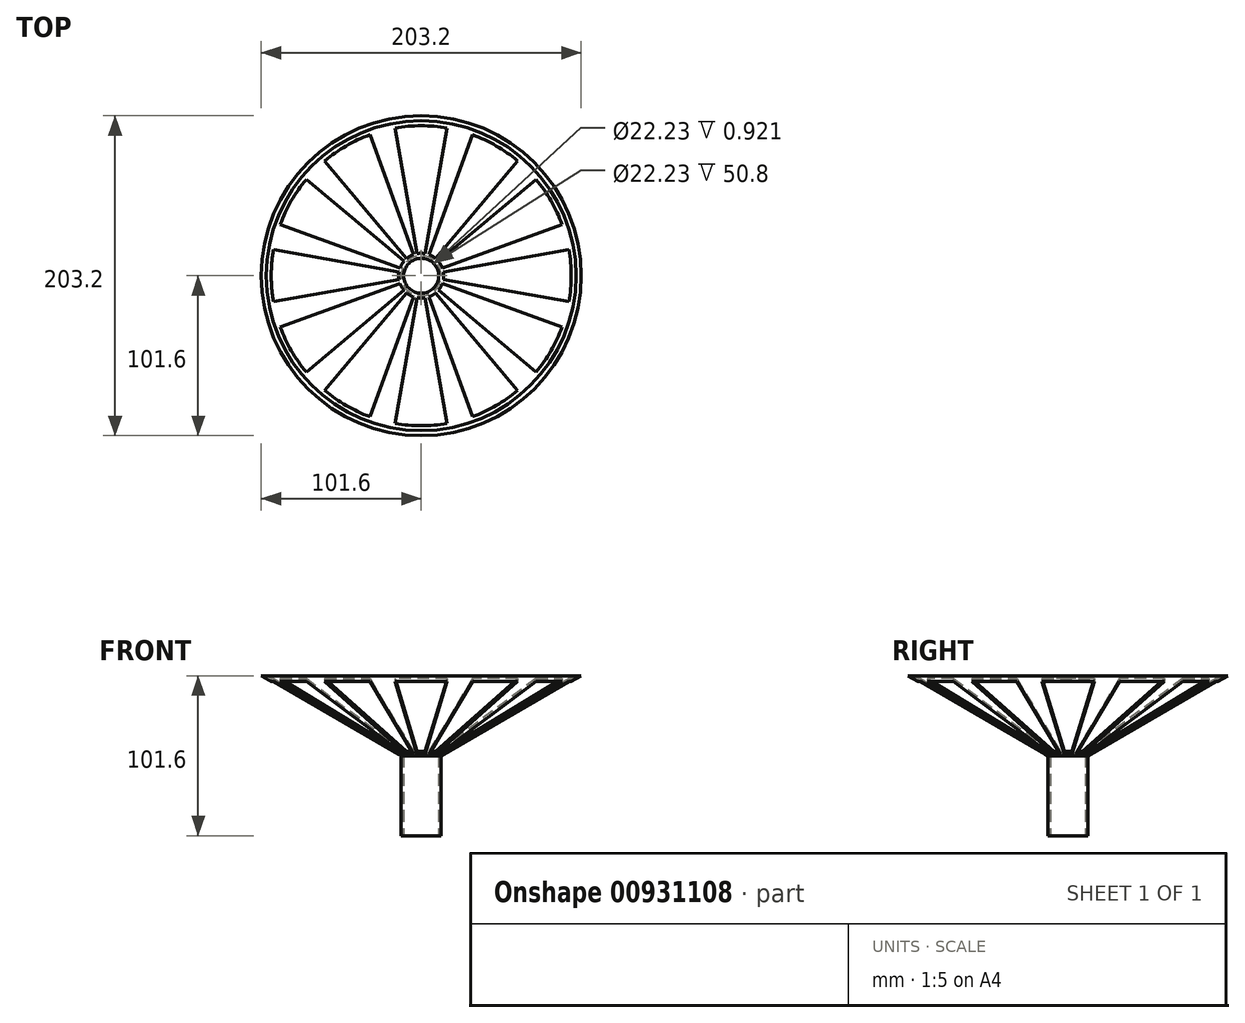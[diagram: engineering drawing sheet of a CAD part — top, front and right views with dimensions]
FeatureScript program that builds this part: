
annotation { "Feature Type Name" : "Feature", "Feature Type Description" : "" }
export const myFeature = defineFeature(function(context is Context, id is Id, definition is map)
    precondition{}
    {
        {
            var Q0;
            Q0=qCreatedBy(makeId("Top.planeOp"),FACE);
            var sketch = newSketch(context, id + "F0", { "sketchPlane" : qUnion([Q0])});
            skCircle(sketch, "E0", {"center": v(0, 0) * mm, "radius": 11.11 * mm});
            skCircle(sketch, "E1", {"center": v(0, 0) * mm, "radius": 12.7 * mm});
            skLineSegment(sketch, "E2", {"start": v(0, 0) * mm, "end": v(0, -95.25) * mm});
            skLineSegment(sketch, "E3", {"start": v(2.48, -14.07) * mm, "end": v(16.54, -93.8) * mm});
            skLineSegment(sketch, "E4", {"start": v(-2.48, -14.07) * mm, "end": v(-16.54, -93.8) * mm});
            skArc(sketch, "E5", {"start": v(-2.48, -14.07) * mm, "mid": v(0, -14.29) * mm, "end": v(2.48, -14.07) * mm});
            skArc(sketch, "E6", {"start": v(-16.54, -93.8) * mm, "mid": v(0, -95.25) * mm, "end": v(16.54, -93.8) * mm});
            skLineSegment(sketch, "E7.1.0", {"start": v(9.18, -10.94) * mm, "end": v(61.23, -72.97) * mm});
            skArc(sketch, "E7.1.1", {"start": v(4.89, -13.43) * mm, "mid": v(7.14, -12.37) * mm, "end": v(9.18, -10.94) * mm});
            skLineSegment(sketch, "E7.1.2", {"start": v(4.89, -13.43) * mm, "end": v(32.58, -89.5) * mm});
            skArc(sketch, "E7.1.3", {"start": v(32.58, -89.5) * mm, "mid": v(47.63, -82.49) * mm, "end": v(61.23, -72.97) * mm});
            skLineSegment(sketch, "E7.2.0", {"start": v(13.43, -4.89) * mm, "end": v(89.5, -32.58) * mm});
            skArc(sketch, "E7.2.1", {"start": v(10.94, -9.18) * mm, "mid": v(12.37, -7.14) * mm, "end": v(13.43, -4.89) * mm});
            skLineSegment(sketch, "E7.2.2", {"start": v(10.94, -9.18) * mm, "end": v(72.97, -61.23) * mm});
            skArc(sketch, "E7.2.3", {"start": v(72.97, -61.23) * mm, "mid": v(82.49, -47.63) * mm, "end": v(89.5, -32.58) * mm});
            skLineSegment(sketch, "E7.3.0", {"start": v(14.07, 2.48) * mm, "end": v(93.8, 16.54) * mm});
            skArc(sketch, "E7.3.1", {"start": v(14.07, -2.48) * mm, "mid": v(14.29, 0) * mm, "end": v(14.07, 2.48) * mm});
            skLineSegment(sketch, "E7.3.2", {"start": v(14.07, -2.48) * mm, "end": v(93.8, -16.54) * mm});
            skArc(sketch, "E7.3.3", {"start": v(93.8, -16.54) * mm, "mid": v(95.25, 0) * mm, "end": v(93.8, 16.54) * mm});
            skLineSegment(sketch, "E7.4.0", {"start": v(10.94, 9.18) * mm, "end": v(72.97, 61.23) * mm});
            skArc(sketch, "E7.4.1", {"start": v(13.43, 4.89) * mm, "mid": v(12.37, 7.14) * mm, "end": v(10.94, 9.18) * mm});
            skLineSegment(sketch, "E7.4.2", {"start": v(13.43, 4.89) * mm, "end": v(89.5, 32.58) * mm});
            skArc(sketch, "E7.4.3", {"start": v(89.5, 32.58) * mm, "mid": v(82.49, 47.62) * mm, "end": v(72.97, 61.23) * mm});
            skLineSegment(sketch, "E7.5.0", {"start": v(4.89, 13.43) * mm, "end": v(32.58, 89.5) * mm});
            skArc(sketch, "E7.5.1", {"start": v(9.18, 10.94) * mm, "mid": v(7.14, 12.37) * mm, "end": v(4.89, 13.43) * mm});
            skLineSegment(sketch, "E7.5.2", {"start": v(9.18, 10.94) * mm, "end": v(61.23, 72.97) * mm});
            skArc(sketch, "E7.5.3", {"start": v(61.23, 72.97) * mm, "mid": v(47.62, 82.49) * mm, "end": v(32.58, 89.5) * mm});
            skLineSegment(sketch, "E8.2.6.0", {"start": v(-2.48, 14.07) * mm, "end": v(-16.54, 93.8) * mm});
            skArc(sketch, "E8.3.6.0", {"start": v(2.48, 14.07) * mm, "mid": v(0, 14.29) * mm, "end": v(-2.48, 14.07) * mm});
            skLineSegment(sketch, "E8.7.6.0", {"start": v(2.48, 14.07) * mm, "end": v(16.54, 93.8) * mm});
            skArc(sketch, "E8.10.6.0", {"start": v(16.54, 93.8) * mm, "mid": v(0, 95.25) * mm, "end": v(-16.54, 93.8) * mm});
            skLineSegment(sketch, "E8.2.7.0", {"start": v(-9.18, 10.94) * mm, "end": v(-61.23, 72.97) * mm});
            skArc(sketch, "E8.3.7.0", {"start": v(-4.89, 13.43) * mm, "mid": v(-7.14, 12.37) * mm, "end": v(-9.18, 10.94) * mm});
            skLineSegment(sketch, "E8.7.7.0", {"start": v(-4.89, 13.43) * mm, "end": v(-32.58, 89.5) * mm});
            skArc(sketch, "E8.10.7.0", {"start": v(-32.58, 89.5) * mm, "mid": v(-47.62, 82.49) * mm, "end": v(-61.23, 72.97) * mm});
            skLineSegment(sketch, "E8.2.8.0", {"start": v(-13.43, 4.89) * mm, "end": v(-89.5, 32.58) * mm});
            skArc(sketch, "E8.3.8.0", {"start": v(-10.94, 9.18) * mm, "mid": v(-12.37, 7.14) * mm, "end": v(-13.43, 4.89) * mm});
            skLineSegment(sketch, "E8.7.8.0", {"start": v(-10.94, 9.18) * mm, "end": v(-72.97, 61.23) * mm});
            skArc(sketch, "E8.10.8.0", {"start": v(-72.97, 61.23) * mm, "mid": v(-82.49, 47.63) * mm, "end": v(-89.5, 32.58) * mm});
            skLineSegment(sketch, "E8.2.9.0", {"start": v(-14.07, -2.48) * mm, "end": v(-93.8, -16.54) * mm});
            skArc(sketch, "E8.3.9.0", {"start": v(-14.07, 2.48) * mm, "mid": v(-14.29, 0) * mm, "end": v(-14.07, -2.48) * mm});
            skLineSegment(sketch, "E8.7.9.0", {"start": v(-14.07, 2.48) * mm, "end": v(-93.8, 16.54) * mm});
            skArc(sketch, "E8.10.9.0", {"start": v(-93.8, 16.54) * mm, "mid": v(-95.25, 0) * mm, "end": v(-93.8, -16.54) * mm});
            skLineSegment(sketch, "E8.2.10.0", {"start": v(-10.94, -9.18) * mm, "end": v(-72.97, -61.23) * mm});
            skArc(sketch, "E8.3.10.0", {"start": v(-13.43, -4.89) * mm, "mid": v(-12.37, -7.14) * mm, "end": v(-10.94, -9.18) * mm});
            skLineSegment(sketch, "E8.7.10.0", {"start": v(-13.43, -4.89) * mm, "end": v(-89.5, -32.58) * mm});
            skArc(sketch, "E8.10.10.0", {"start": v(-89.5, -32.58) * mm, "mid": v(-82.49, -47.63) * mm, "end": v(-72.97, -61.23) * mm});
            skLineSegment(sketch, "E8.2.11.0", {"start": v(-4.89, -13.43) * mm, "end": v(-32.58, -89.5) * mm});
            skArc(sketch, "E8.3.11.0", {"start": v(-9.18, -10.94) * mm, "mid": v(-7.14, -12.37) * mm, "end": v(-4.89, -13.43) * mm});
            skLineSegment(sketch, "E8.7.11.0", {"start": v(-9.18, -10.94) * mm, "end": v(-61.23, -72.97) * mm});
            skArc(sketch, "E8.10.11.0", {"start": v(-61.23, -72.97) * mm, "mid": v(-47.63, -82.49) * mm, "end": v(-32.58, -89.5) * mm});
            skSolve(sketch);
        }
        {
            var Q0;
            Q0=makeQuery(id+"F0.imprint","IMPRINT",FACE,{"disambiguationData":[TD([[makeQuery(id+"F0.imprint","IMPRINT",EDGE,{"derivedFrom":sQuery(id+"F0.wireOp",EDGE,"E0")}),-1.0]])]});
            extrude(context, id + "F1", {"entities" : qUnion([Q0]), "depth" : 50.8 * mm, "offsetDistance" : 25.4 * mm});
        }
        {
            var Q0;
            Q0=qCreatedBy(makeId("Front.planeOp"),FACE);
            var sketch = newSketch(context, id + "F2", { "sketchPlane" : qUnion([Q0])});
            skLineSegment(sketch, "E9", {"start": v(0, 0) * mm, "end": v(0, 50.8) * mm});
            skLineSegment(sketch, "E10", {"start": v(0, 50.8) * mm, "end": v(11.11, 50.8) * mm});
            skLineSegment(sketch, "E11", {"start": v(11.11, 50.8) * mm, "end": v(12.7, 50.8) * mm});
            skLineSegment(sketch, "E12.top", {"start": v(0, 101.6) * mm, "end": v(11.11, 101.6) * mm});
            skLineSegment(sketch, "E12.left", {"start": v(0, 50.8) * mm, "end": v(0, 101.6) * mm});
            skLineSegment(sketch, "E12.right", {"start": v(11.11, 50.8) * mm, "end": v(11.11, 101.6) * mm});
            skLineSegment(sketch, "E13", {"start": v(11.11, 101.6) * mm, "end": v(101.6, 101.6) * mm});
            skLineSegment(sketch, "E14", {"start": v(101.6, 101.6) * mm, "end": v(12.7, 50.8) * mm});
            skLineSegment(sketch, "E15.0", {"start": v(98.4, 101.6) * mm, "end": v(11.11, 51.72) * mm});
            skSolve(sketch);
        }
        {
            var Q0;
            {var subQ4=sQuery(id+"F2.wireOp",EDGE,"E11");Q0=makeQuery(id+"F2.imprint","IMPRINT",FACE,{"disambiguationData":[TD([[makeQuery(id+"F2.imprint","IMPRINT",EDGE,{"derivedFrom":subQ4}),1.0]])]});}
            var Q1;
            Q1=sQuery(id+"F2.wireOp",EDGE,"E12.left");
            revolve(context, id + "F3", {"surfaceOperationType" : NewSurfaceOperationType.NEW, "entities" : qUnion([Q0]), "axis" : qUnion([Q1]), "revolveType" : RevolveType.FULL});
        }
        {
            var Q0;
            Q0=makeQuery(id+"F0.imprint","IMPRINT",FACE,{"disambiguationData":[TD([[makeQuery(id+"F0.imprint","IMPRINT",EDGE,{"derivedFrom":sQuery(id+"F0.wireOp",EDGE,"E7.4.0")}),-1.0]])]});
            var Q1;
            Q1=makeQuery(id+"F0.imprint","IMPRINT",FACE,{"disambiguationData":[TD([[makeQuery(id+"F0.imprint","IMPRINT",EDGE,{"derivedFrom":sQuery(id+"F0.wireOp",EDGE,"E7.3.0")}),-1.0]])]});
            var Q2;
            Q2=makeQuery(id+"F0.imprint","IMPRINT",FACE,{"disambiguationData":[TD([[makeQuery(id+"F0.imprint","IMPRINT",EDGE,{"derivedFrom":sQuery(id+"F0.wireOp",EDGE,"E7.5.0")}),-1.0]])]});
            var Q3;
            {var subQ5=sQuery(id+"F0.wireOp",EDGE,"E4");Q3=makeQuery(id+"F0.imprint","IMPRINT",FACE,{"disambiguationData":[TD([[makeQuery(id+"F0.imprint","IMPRINT",EDGE,{"derivedFrom":subQ5}),1.0]])]});}
            var Q4;
            {var subQ5=sQuery(id+"F0.wireOp",EDGE,"E3");Q4=makeQuery(id+"F0.imprint","IMPRINT",FACE,{"disambiguationData":[TD([[makeQuery(id+"F0.imprint","IMPRINT",EDGE,{"derivedFrom":subQ5}),-1.0]])]});}
            var Q5;
            Q5=makeQuery(id+"F0.imprint","IMPRINT",FACE,{"disambiguationData":[TD([[makeQuery(id+"F0.imprint","IMPRINT",EDGE,{"derivedFrom":sQuery(id+"F0.wireOp",EDGE,"E7.1.0")}),-1.0]])]});
            var Q6;
            Q6=makeQuery(id+"F0.imprint","IMPRINT",FACE,{"disambiguationData":[TD([[makeQuery(id+"F0.imprint","IMPRINT",EDGE,{"derivedFrom":sQuery(id+"F0.wireOp",EDGE,"E7.2.0")}),-1.0]])]});
            var Q7;
            Q7=makeQuery(id+"F0.imprint","IMPRINT",FACE,{"disambiguationData":[TD([[makeQuery(id+"F0.imprint","IMPRINT",EDGE,{"derivedFrom":sQuery(id+"F0.wireOp",EDGE,"E8.2.11.0")}),-1.0]])]});
            var Q8;
            Q8=makeQuery(id+"F0.imprint","IMPRINT",FACE,{"disambiguationData":[TD([[makeQuery(id+"F0.imprint","IMPRINT",EDGE,{"derivedFrom":sQuery(id+"F0.wireOp",EDGE,"E8.2.10.0")}),-1.0]])]});
            var Q9;
            Q9=makeQuery(id+"F0.imprint","IMPRINT",FACE,{"disambiguationData":[TD([[makeQuery(id+"F0.imprint","IMPRINT",EDGE,{"derivedFrom":sQuery(id+"F0.wireOp",EDGE,"E8.2.9.0")}),-1.0]])]});
            var Q10;
            Q10=makeQuery(id+"F0.imprint","IMPRINT",FACE,{"disambiguationData":[TD([[makeQuery(id+"F0.imprint","IMPRINT",EDGE,{"derivedFrom":sQuery(id+"F0.wireOp",EDGE,"E8.2.8.0")}),-1.0]])]});
            var Q11;
            Q11=makeQuery(id+"F0.imprint","IMPRINT",FACE,{"disambiguationData":[TD([[makeQuery(id+"F0.imprint","IMPRINT",EDGE,{"derivedFrom":sQuery(id+"F0.wireOp",EDGE,"E8.2.6.0")}),-1.0]])]});
            var Q12;
            Q12=makeQuery(id+"F0.imprint","IMPRINT",FACE,{"disambiguationData":[TD([[makeQuery(id+"F0.imprint","IMPRINT",EDGE,{"derivedFrom":sQuery(id+"F0.wireOp",EDGE,"E8.2.7.0")}),-1.0]])]});
            extrude(context, id + "F4", {"entities" : qUnion([Q0, Q1, Q2, Q3, Q4, Q5, Q6, Q7, Q8, Q9, Q10, Q11, Q12]), "operationType" : NewBodyOperationType.REMOVE, "depth" : 152.4 * mm, "offsetDistance" : 25.4 * mm});
        }
    });
